# Revit family: RESERVOIR DE VIDE
name_source: partatom
category: Equipement de génie climatique
revit_build: Autodesk Revit 2018 (Build: 20170223_1515(x64)
units: mm (PartAtom-declared; Revit-internal decimal feet)

## family parameters
Basée sur le plan de construction = Non
Classification = Aucun
Cote de connecteur circulaire = Utiliser le diamètre
Couper avec des vides une fois chargée = Non
Partagée = Non
Point de calcul de pièce = Non
Toujours verticalement = Oui
Type d'élément = Normal

## types (3) — shared parameters
BRANCHEMENT_TERRE = Oui
DEBIT_ASPI_VIDE = 0.0 m³/h
DESCRIPTION_PURGE = G1/2"
EP_PATTE = 5 mm  [stored 0.0164042 ft]
Fabricant = MIL'S
HAUT_LEVAGE = 52.4 mm
LARG_PATTE = 80 mm  [stored 0.262467 ft]
LONG_BOSS = 25 mm  [stored 0.082021 ft]
LONG_BOSS_BAS = 20 mm  [stored 0.0656168 ft]
RAYON_PATTE = 375 mm  [stored 1.23031 ft]
ØBOSS_2 = 17.5 mm  [stored 0.0574147 ft]
ØBOSS_BAS = 26.5 mm  [stored 0.0869423 ft]
ØPATTE = 750 mm

## per-type parameters (varying)
- 500L-VIDE: DESCRIPTION_CANA=G1"1/4; DIAMETRE=650 mm; DIAM_ASPI_VIDE=32 mm  [stored 0.104987 ft]; DIAM_PURGE=0 mm  [stored 0 ft]; EP_BOUCH=5 mm  [stored 0.0164042 ft]; HAUTEUR=1815 mm; HAUT_FOND=148.5 mm  [stored 0.487205 ft]; HAUT_VIROLE_PIED=264 mm  [stored 0.866142 ft]; LONG_BOUCH=15 mm  [stored 0.0492126 ft]; LONG_OUVERTURE=194.5 mm; LONG_VIROLE=1320 mm; OFFSET_BOSS=338 mm  [stored 1.10892 ft]; OFFSET_BOSS_BAS=180 mm  [stored 0.590551 ft]; OFFSET_HAUT_BOSS_1=872 mm; OFFSET_HAUT_BOSS_2=1323 mm; OFFSET_HAUT_BOSS_3=1472 mm; OFFSET_HAUT_FOND=196.5 mm  [stored 0.644685 ft]; OFFSET_PATTE_EXT=325 mm  [stored 1.06627 ft]; OFFSET_PATTE_INT=225 mm  [stored 0.738189 ft]; PIEDS_1000L=Non; PIEDS_2000L=Non; PIEDS_500L=Oui; POIDS(Kg)=120 mm  [stored 0.393701 ft]; RAY_BOUCH=25 mm  [stored 0.082021 ft]; RAY_PAN_BOUCH=15.6 mm  [stored 0.0511811 ft]; TAILLE_VANNE=Vanne BS FF : DN32 - G1"1/4 - FF (231 0005); ØBOSS=50 mm  [stored 0.164042 ft]; ØVIROLE=650 mm; ØVIROLE_BAS=550 mm; ØVIROLE_BAS_INT=544 mm
- 1000L-VIDE: DESCRIPTION_CANA=G1"1/2; DIAMETRE=850 mm; DIAM_ASPI_VIDE=40 mm  [stored 0.131234 ft]; DIAM_PURGE=0 mm  [stored 0 ft]; EP_BOUCH=5 mm  [stored 0.0164042 ft]; HAUTEUR=1800 mm; HAUT_FOND=184.5 mm; HAUT_VIROLE_PIED=259 mm  [stored 0.849738 ft]; LONG_BOUCH=15 mm  [stored 0.0492126 ft]; LONG_OUVERTURE=255 mm  [stored 0.836614 ft]; LONG_VIROLE=1280 mm; OFFSET_BOSS=438 mm; OFFSET_BOSS_BAS=180 mm  [stored 0.590551 ft]; OFFSET_HAUT_BOSS_1=850 mm; OFFSET_HAUT_BOSS_2=1300 mm; OFFSET_HAUT_BOSS_3=1488 mm; OFFSET_HAUT_FOND=174 mm  [stored 0.570866 ft]; OFFSET_PATTE_EXT=410 mm  [stored 1.34514 ft]; OFFSET_PATTE_INT=310 mm  [stored 1.01706 ft]; PIEDS_1000L=Oui; PIEDS_2000L=Non; PIEDS_500L=Non; POIDS(Kg)=210 mm  [stored 0.688976 ft]; RAY_BOUCH=33 mm  [stored 0.108268 ft]; RAY_PAN_BOUCH=15.6 mm  [stored 0.0511811 ft]; TAILLE_VANNE=Vanne BS FF : DN40 - G1"1/2 - FF (231 0009); ØBOSS=66 mm  [stored 0.216535 ft]; ØVIROLE=850 mm; ØVIROLE_BAS=720 mm; ØVIROLE_BAS_INT=714 mm
- 2000L-VIDE: DESCRIPTION_CANA=G2"; DIAMETRE=1200 mm; DIAM_ASPI_VIDE=50 mm  [stored 0.164042 ft]; DIAM_PURGE=25 mm  [stored 0.082021 ft]; EP_BOUCH=6.3 mm; HAUTEUR=2100 mm; HAUT_FOND=260 mm  [stored 0.853018 ft]; HAUT_VIROLE_PIED=296 mm  [stored 0.971129 ft]; LONG_BOUCH=19 mm  [stored 0.062336 ft]; LONG_OUVERTURE=255 mm  [stored 0.836614 ft]; LONG_VIROLE=1390 mm; OFFSET_BOSS=438 mm; OFFSET_BOSS_BAS=127 mm; OFFSET_HAUT_BOSS_1=850 mm; OFFSET_HAUT_BOSS_2=1300 mm; OFFSET_HAUT_BOSS_3=1600 mm; OFFSET_HAUT_FOND=140 mm  [stored 0.459318 ft]; OFFSET_PATTE_EXT=637.5 mm; OFFSET_PATTE_INT=537.5 mm; PIEDS_1000L=Non; PIEDS_2000L=Oui; PIEDS_500L=Non; POIDS(Kg)=340 mm  [stored 1.11549 ft]; RAY_BOUCH=33 mm  [stored 0.108268 ft]; RAY_PAN_BOUCH=19.8 mm  [stored 0.0649606 ft]; TAILLE_VANNE=Vanne BS FF : DN32 - G1"1/4 - FF (231 0005); ØBOSS=66 mm  [stored 0.216535 ft]; ØVIROLE=1200 mm; ØVIROLE_BAS=1105 mm; ØVIROLE_BAS_INT=1099 mm

note: [stored X ft] marks values corroborated as IEEE doubles in the binary element streams (Revit-internal decimal feet)

## geometry (parser evidence)
native form markers: Sweep x7
no freeform markers — native parametric forms only
